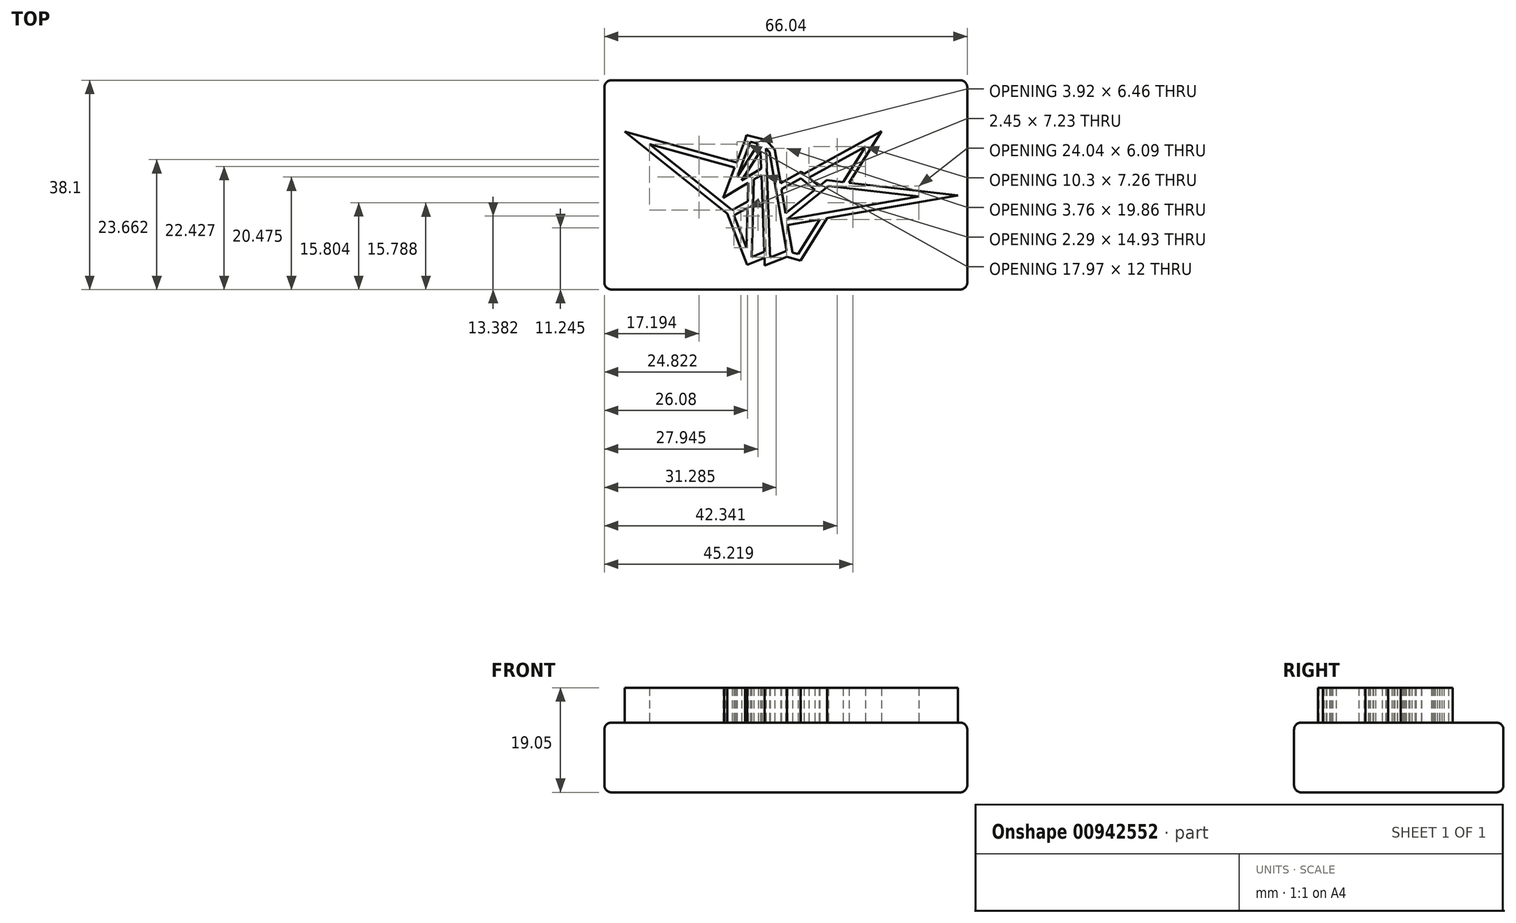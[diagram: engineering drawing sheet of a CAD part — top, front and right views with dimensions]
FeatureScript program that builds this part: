
annotation { "Feature Type Name" : "Feature", "Feature Type Description" : "" }
export const myFeature = defineFeature(function(context is Context, id is Id, definition is map)
    precondition{}
    {
        {
            var Q0;
            Q0=qCreatedBy(makeId("Top.planeOp"),FACE);
            var sketch = newSketch(context, id + "F0", { "sketchPlane" : qUnion([Q0])});
            skLineSegment(sketch, "E0.bottom", {"start": v(-31.75, 19.05) * mm, "end": v(34.3, 19.05) * mm});
            skLineSegment(sketch, "E0.top", {"start": v(-31.75, -19.05) * mm, "end": v(34.3, -19.05) * mm});
            skLineSegment(sketch, "E0.left", {"start": v(-31.75, 19.05) * mm, "end": v(-31.75, -19.05) * mm});
            skLineSegment(sketch, "E0.right", {"start": v(34.3, 19.05) * mm, "end": v(34.3, -19.05) * mm});
            skSolve(sketch);
        }
        {
            var Q0;
            Q0=makeQuery(id+"F0.imprint","IMPRINT",FACE,{"disambiguationData":[TD([[makeQuery(id+"F0.imprint","IMPRINT",EDGE,{"derivedFrom":sQuery(id+"F0.wireOp",EDGE,"E0.bottom")}),-1.0]])]});
            extrude(context, id + "F1", {"entities" : qUnion([Q0]), "depth" : 12.7 * mm, "offsetDistance" : 25.4 * mm});
        }
        {
            var Q0;
            Q0=makeQuery(id+"F1.opExtrude","CAP_FACE",FACE,{"disambiguationData":[OSD([sQuery(id+"F0.wireOp",EDGE,"E0.bottom"),sQuery(id+"F0.wireOp",EDGE,"E0.top"),sQuery(id+"F0.wireOp",EDGE,"E0.left"),sQuery(id+"F0.wireOp",EDGE,"E0.right")])],"isStart":false});
            var sketch = newSketch(context, id + "F2", { "sketchPlane" : qUnion([Q0])});
            skLineSegment(sketch, "E1", {"start": v(-23.54, 7.42) * mm, "end": v(-8.51, -4.57) * mm});
            skLineSegment(sketch, "E2", {"start": v(-8.15, -5.53) * mm, "end": v(-5.91, -11.42) * mm});
            skLineSegment(sketch, "E3", {"start": v(3.49, -12.6) * mm, "end": v(7.44, -6.28) * mm});
            skLineSegment(sketch, "E4", {"start": v(15.74, 7) * mm, "end": v(5.44, 1.3) * mm});
            skLineSegment(sketch, "E5", {"start": v(1.41, -12.02) * mm, "end": v(-1.7, 5.96) * mm});
            skLineSegment(sketch, "E6", {"start": v(-23.54, 7.42) * mm, "end": v(-8.05, 3.17) * mm});
            skLineSegment(sketch, "E7", {"start": v(-3.7, 7.48) * mm, "end": v(-5.22, 7.84) * mm});
            skLineSegment(sketch, "E8", {"start": v(-5.22, 7.84) * mm, "end": v(-7.63, 1.38) * mm});
            skLineSegment(sketch, "E9", {"start": v(-6.79, 0.82) * mm, "end": v(-3.22, 2.96) * mm});
            skLineSegment(sketch, "E10", {"start": v(-2.57, -14.66) * mm, "end": v(-2.62, -13.26) * mm});
            skLineSegment(sketch, "E11", {"start": v(-8.51, -4.57) * mm, "end": v(-5.67, -3.01) * mm});
            skLineSegment(sketch, "E12.trimOffspring", {"start": v(11.68, 0.51) * mm, "end": v(15.74, 7) * mm});
            skLineSegment(sketch, "E13.0", {"start": v(-9.36, -5.2) * mm, "end": v(-6.17, -13.6) * mm});
            skLineSegment(sketch, "E14.0", {"start": v(-8.04, -5.47) * mm, "end": v(-5.7, -4.2) * mm});
            skLineSegment(sketch, "E15.0", {"start": v(-4.95, -13.13) * mm, "end": v(-4.54, 0.98) * mm});
            skLineSegment(sketch, "E16.0", {"start": v(-6.17, 8.2) * mm, "end": v(-7.7, 4.12) * mm});
            skLineSegment(sketch, "E17.0", {"start": v(-2.35, 8.2) * mm, "end": v(-4.99, 8.83) * mm});
            skLineSegment(sketch, "E18.0", {"start": v(-1.65, -12.14) * mm, "end": v(-2.34, 6.67) * mm});
            skLineSegment(sketch, "E19.0", {"start": v(18.52, 9.71) * mm, "end": v(4.6, 2) * mm});
            skLineSegment(sketch, "E20.0", {"start": v(12.8, 0.38) * mm, "end": v(18.68, 9.8) * mm});
            skLineSegment(sketch, "E21.0", {"start": v(3.95, -13.78) * mm, "end": v(8.78, -6.05) * mm});
            skLineSegment(sketch, "E22.trimOffspring", {"start": v(-8.05, 3.17) * mm, "end": v(-9.7, -1.23) * mm});
            skLineSegment(sketch, "E23.trimOffspring", {"start": v(-3.22, 2.96) * mm, "end": v(-3.34, 6.17) * mm});
            skLineSegment(sketch, "E24", {"start": v(-6.17, 8.2) * mm, "end": v(-5.9, 9.05) * mm});
            skLineSegment(sketch, "E25", {"start": v(-4.99, 8.83) * mm, "end": v(-5.9, 9.05) * mm});
            skLineSegment(sketch, "E26", {"start": v(18.52, 9.71) * mm, "end": v(18.68, 9.8) * mm});
            skLineSegment(sketch, "E27.trimOffspring", {"start": v(1.28, -5.32) * mm, "end": v(1.29, -5.3) * mm});
            skLineSegment(sketch, "E28.0", {"start": v(-23.47, 8.46) * mm, "end": v(-7.78, 4.15) * mm});
            skLineSegment(sketch, "E29.0", {"start": v(-24.32, 6.74) * mm, "end": v(-9.93, -4.74) * mm});
            skLineSegment(sketch, "E30.0", {"start": v(-5.91, -11.42) * mm, "end": v(-5.7, -4.2) * mm});
            skLineSegment(sketch, "E31", {"start": v(-3.7, 7.48) * mm, "end": v(-7.63, 1.38) * mm});
            skLineSegment(sketch, "E32.0", {"start": v(-3.34, 6.17) * mm, "end": v(-6.79, 0.82) * mm});
            skLineSegment(sketch, "E33.0", {"start": v(-6.76, -0.35) * mm, "end": v(-5.57, 0.36) * mm});
            skLineSegment(sketch, "E34", {"start": v(-9.93, -4.74) * mm, "end": v(-9.36, -5.2) * mm});
            skLineSegment(sketch, "E35", {"start": v(-8.04, -5.47) * mm, "end": v(-8.15, -5.53) * mm});
            skLineSegment(sketch, "E36", {"start": v(-24.32, 6.74) * mm, "end": v(-28.04, 9.71) * mm});
            skLineSegment(sketch, "E37", {"start": v(-23.47, 8.46) * mm, "end": v(-28.04, 9.71) * mm});
            skLineSegment(sketch, "E38", {"start": v(-7.78, 4.15) * mm, "end": v(-7.7, 4.12) * mm});
            skLineSegment(sketch, "E39.trimOffspring", {"start": v(-4.54, 0.98) * mm, "end": v(-3.18, 1.8) * mm});
            skLineSegment(sketch, "E40", {"start": v(-6.76, -0.35) * mm, "end": v(-10.15, -2.37) * mm});
            skLineSegment(sketch, "E41", {"start": v(-9.7, -1.23) * mm, "end": v(-10.15, -2.37) * mm});
            skLineSegment(sketch, "E42.0", {"start": v(1.28, -5.32) * mm, "end": v(1.28, -5.32) * mm});
            skLineSegment(sketch, "E43", {"start": v(-6.17, -13.6) * mm, "end": v(-5.76, -14.58) * mm});
            skLineSegment(sketch, "E44.trimOffspring", {"start": v(-5.67, -3.01) * mm, "end": v(-5.57, 0.36) * mm});
            skLineSegment(sketch, "E45.0", {"start": v(2.5, -12.33) * mm, "end": v(1.62, -7.3) * mm});
            skLineSegment(sketch, "E46", {"start": v(-2.35, 8.2) * mm, "end": v(-0.76, 6.43) * mm});
            skLineSegment(sketch, "E47.0", {"start": v(-2.34, 6.67) * mm, "end": v(-1.7, 5.96) * mm});
            skLineSegment(sketch, "E48", {"start": v(-5.76, -14.58) * mm, "end": v(-2.62, -13.26) * mm});
            skLineSegment(sketch, "E49.0", {"start": v(-4.95, -13.13) * mm, "end": v(-3.01, -12.32) * mm});
            skLineSegment(sketch, "E50", {"start": v(-3.01, -12.32) * mm, "end": v(-2.66, -12.17) * mm});
            skLineSegment(sketch, "E51", {"start": v(-2.57, -14.66) * mm, "end": v(1.46, -13.1) * mm});
            skLineSegment(sketch, "E52", {"start": v(3.95, -13.78) * mm, "end": v(1.46, -13.1) * mm});
            skLineSegment(sketch, "E53.0", {"start": v(-1.59, -13.2) * mm, "end": v(1.41, -12.02) * mm});
            skLineSegment(sketch, "E54.trimOffspring", {"start": v(-2.66, -12.17) * mm, "end": v(-3.18, 1.8) * mm});
            skLineSegment(sketch, "E55.0", {"start": v(3.49, -12.6) * mm, "end": v(2.5, -12.33) * mm});
            skLineSegment(sketch, "E56", {"start": v(-1.65, -12.14) * mm, "end": v(-1.59, -13.2) * mm});
            skLineSegment(sketch, "E57.trimOffspring", {"start": v(1.28, -5.32) * mm, "end": v(1.28, -5.32) * mm});
            skLineSegment(sketch, "E58", {"start": v(4.1, 2.4) * mm, "end": v(4.6, 2) * mm});
            skLineSegment(sketch, "E59", {"start": v(1.45, -6.29) * mm, "end": v(25.49, -2.12) * mm});
            skLineSegment(sketch, "E60.0", {"start": v(4, 1.18) * mm, "end": v(6.53, -0.9) * mm});
            skLineSegment(sketch, "E61", {"start": v(9.03, -0.2) * mm, "end": v(1.45, -6.29) * mm});
            skLineSegment(sketch, "E62.0", {"start": v(8.73, 0.86) * mm, "end": v(7.34, -0.25) * mm});
            skLineSegment(sketch, "E63.trimOffspring", {"start": v(9.03, -0.2) * mm, "end": v(25.49, -2.12) * mm});
            skLineSegment(sketch, "E64.trimOffspring", {"start": v(6.53, -0.9) * mm, "end": v(1.25, -5.15) * mm});
            skLineSegment(sketch, "E65.0", {"start": v(1.6, -7.3) * mm, "end": v(7.44, -6.28) * mm});
            skLineSegment(sketch, "E66.0", {"start": v(9.14, 0.8) * mm, "end": v(11.68, 0.51) * mm});
            skLineSegment(sketch, "E67", {"start": v(26.51, -1.21) * mm, "end": v(32.57, -1.92) * mm});
            skLineSegment(sketch, "E68", {"start": v(9.14, 0.8) * mm, "end": v(8.72, 0.86) * mm});
            skLineSegment(sketch, "E69.trimOffspring", {"start": v(12.8, 0.38) * mm, "end": v(26.51, -1.21) * mm});
            skLineSegment(sketch, "E70.trimOffspring", {"start": v(8.78, -6.05) * mm, "end": v(32.57, -1.92) * mm});
            skLineSegment(sketch, "E71.trimOffspring", {"start": v(1.28, -5.32) * mm, "end": v(1.28, -5.32) * mm});
            skLineSegment(sketch, "E72.trimOffspring", {"start": v(1.25, -5.15) * mm, "end": v(0.5, -0.76) * mm});
            skLineSegment(sketch, "E73.trimOffspring", {"start": v(5.44, 1.3) * mm, "end": v(7.34, -0.25) * mm});
            skLineSegment(sketch, "E74.trimOffspring", {"start": v(0.3, 0.3) * mm, "end": v(4.1, 2.4) * mm});
            skLineSegment(sketch, "E75.trimOffspring", {"start": v(0.5, -0.76) * mm, "end": v(4, 1.18) * mm});
            skLineSegment(sketch, "E76.trimOffspring", {"start": v(0.3, 0.3) * mm, "end": v(-0.76, 6.43) * mm});
            skSolve(sketch);
        }
        {
            var Q0;
            Q0=makeQuery(id+"F2.imprint","IMPRINT",FACE,{"disambiguationData":[TD([[makeQuery(id+"F2.imprint","IMPRINT",EDGE,{"derivedFrom":sQuery(id+"F2.wireOp",EDGE,"E1")}),-1.0]])]});
            extrude(context, id + "F3", {"entities" : qUnion([Q0]), "depth" : 6.35 * mm, "offsetDistance" : 25.4 * mm});
        }
        {
            var Q0;
            Q0=makeQuery(id+"F1.opExtrude","CAP_EDGE",EDGE,{"disambiguationData":[OSD([sQuery(id+"F0.wireOp",EDGE,"E0.left")])],"isStart":false});
            var Q1;
            Q1=makeQuery(id+"F1.opExtrude","CAP_EDGE",EDGE,{"disambiguationData":[OSD([sQuery(id+"F0.wireOp",EDGE,"E0.top")])],"isStart":false});
            var Q2;
            Q2=makeQuery(id+"F1.opExtrude","CAP_EDGE",EDGE,{"disambiguationData":[OSD([sQuery(id+"F0.wireOp",EDGE,"E0.right")])],"isStart":false});
            var Q3;
            Q3=makeQuery(id+"F1.opExtrude","CAP_EDGE",EDGE,{"disambiguationData":[OSD([sQuery(id+"F0.wireOp",EDGE,"E0.bottom")])],"isStart":false});
            var Q4;
            Q4=makeQuery(id+"F1.opExtrude","CAP_EDGE",EDGE,{"disambiguationData":[OSD([sQuery(id+"F0.wireOp",EDGE,"E0.top")])],"isStart":true});
            var Q5;
            Q5=makeQuery(id+"F1.opExtrude","CAP_EDGE",EDGE,{"disambiguationData":[OSD([sQuery(id+"F0.wireOp",EDGE,"E0.left")])],"isStart":true});
            var Q6;
            Q6=makeQuery(id+"F1.opExtrude","CAP_EDGE",EDGE,{"disambiguationData":[OSD([sQuery(id+"F0.wireOp",EDGE,"E0.bottom")])],"isStart":true});
            var Q7;
            Q7=makeQuery(id+"F1.opExtrude","CAP_EDGE",EDGE,{"disambiguationData":[OSD([sQuery(id+"F0.wireOp",EDGE,"E0.right")])],"isStart":true});
            var Q8;
            Q8=makeQuery(id+"F1.opExtrude","SWEPT_EDGE",EDGE,{"disambiguationData":[OSD([sQuery(id+"F0.wireOp",EDGE,"E0.top"),sQuery(id+"F0.wireOp",EDGE,"E0.right")])]});
            var Q9;
            Q9=makeQuery(id+"F1.opExtrude","SWEPT_EDGE",EDGE,{"disambiguationData":[OSD([sQuery(id+"F0.wireOp",EDGE,"E0.bottom"),sQuery(id+"F0.wireOp",EDGE,"E0.right")])]});
            var Q10;
            Q10=makeQuery(id+"F1.opExtrude","SWEPT_EDGE",EDGE,{"disambiguationData":[OSD([sQuery(id+"F0.wireOp",EDGE,"E0.bottom"),sQuery(id+"F0.wireOp",EDGE,"E0.left")])]});
            var Q11;
            Q11=makeQuery(id+"F1.opExtrude","SWEPT_EDGE",EDGE,{"disambiguationData":[OSD([sQuery(id+"F0.wireOp",EDGE,"E0.top"),sQuery(id+"F0.wireOp",EDGE,"E0.left")])]});
            fillet(context, id + "F4", {"entities" : qUnion([Q0, Q1, Q2, Q3, Q4, Q5, Q6, Q7, Q8, Q9, Q10, Q11]), "radius" : 1.27 * mm, "tangentPropagation" : true, "allowEdgeOverflow" : false});
        }
    });
